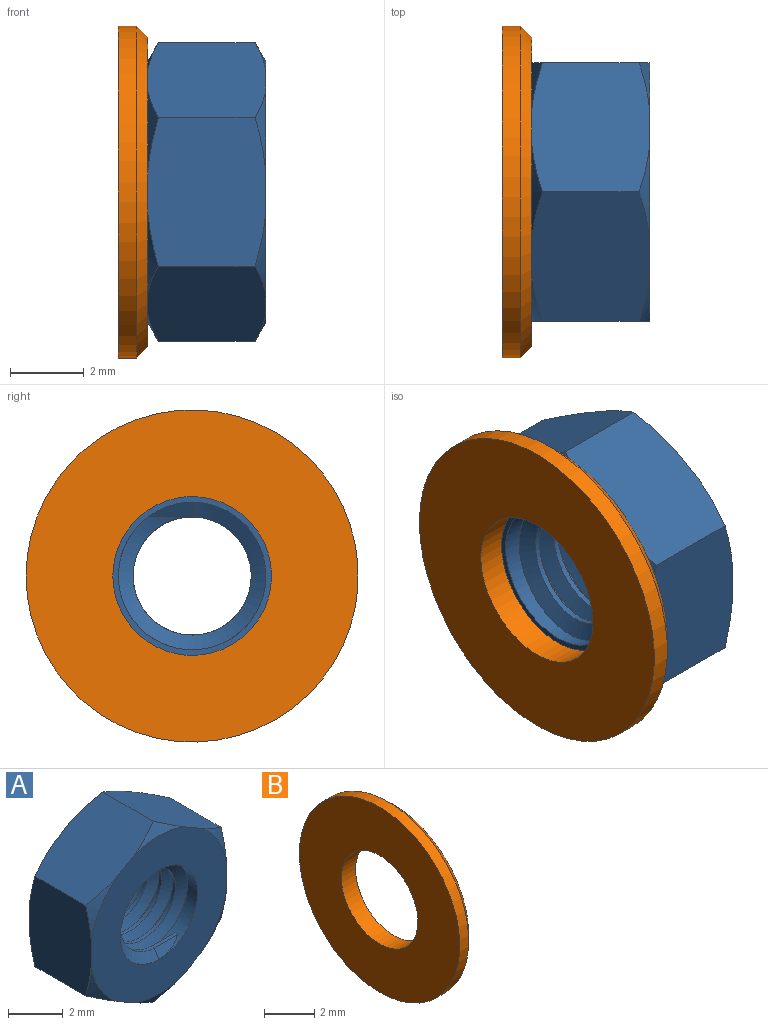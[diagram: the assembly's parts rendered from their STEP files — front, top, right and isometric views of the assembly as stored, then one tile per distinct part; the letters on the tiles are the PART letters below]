
ASSEMBLY  parts=2 mates=1
PART A: 28 faces, bbox 8.2x3.5x8.3 mm
  f0: cone r=3.54mm half-angle=60deg, axis (0,-1,0), area 0.8mm2, adj f11,f22,f23
  f1: cone r=3.54mm half-angle=60deg, axis (0,-1,0), area 0.8mm2, adj f11,f23,f24
  f2: cone r=3.54mm half-angle=60deg, axis (0,-1,0), area 0.8mm2, adj f11,f24,f25
  f3: cone r=3.54mm half-angle=60deg, axis (0,-1,0), area 0.8mm2, adj f11,f25,f26
  f4: cone r=3.54mm half-angle=60deg, axis (0,-1,0), area 0.8mm2, adj f11,f22,f27
  f5: cone r=4.04mm half-angle=60deg, axis (0,1,0), area 0.8mm2, adj f10,f22,f23
  f6: cone r=4.04mm half-angle=60deg, axis (0,1,0), area 0.8mm2, adj f10,f23,f24
  f7: cone r=4.04mm half-angle=60deg, axis (0,1,0), area 0.8mm2, adj f10,f24,f25
  f8: cone r=4.04mm half-angle=60deg, axis (0,1,0), area 0.8mm2, adj f10,f25,f26
  f9: cone r=4.04mm half-angle=60deg, axis (0,1,0), area 0.8mm2, adj f10,f26,f27
  f10: plane 7.08x7mm, normal (0,-1,0), area 26.7mm2, adj f5,f6,f7,f8,f9,f12,f21,f22
  f11: plane 7.08x7mm, normal (0,1,0), area 26.7mm2, adj f0,f1,f2,f3,f4,f12,f20,f22
  f12: cylinder r=2mm len=4mm, axis (0,1,0), area 11.1mm2, adj f10,f11,f13,f15,f16,f17,f18,f19
  f13: plane 0.62x0.38mm, normal (0.35,0,-0.94), area 0.2mm2, adj f12,f14,f15,f16
  f14: cylinder r=1.6mm len=3.2mm, axis (0,1,0), area 5.7mm2, adj f13,f15,f16,f17
  f15: bspline ~4.62x4mm, area 19.3mm2, adj f12,f13,f14,f18
  f16: bspline ~4.62x4mm, area 19.3mm2, adj f12,f13,f14,f19
  f17: plane 1.2x0.15mm, normal (0,0,1), area 0.2mm2, adj f12,f14,f18,f19
  f18: plane 1.31x0.51mm, normal (0,0.87,0.5), area 0.4mm2, adj f12,f15,f17
  f19: plane 1.31x0.51mm, normal (0,-0.87,0.5), area 0.4mm2, adj f12,f16,f17
  f20: cone r=3.54mm half-angle=60deg, axis (0,-1,0), area 0.8mm2, adj f11,f26,f27
  f21: cone r=4.04mm half-angle=60deg, axis (0,1,0), area 0.8mm2, adj f10,f22,f27
  f22: plane 3.68x3.38mm, normal (-0.5,0,0.87), area 12.2mm2, adj f0,f4,f5,f10,f11,f21,f23,f27
  f23: plane 3.68x3.38mm, normal (0.5,0,0.87), area 12.2mm2, adj f0,f1,f5,f6,f10,f11,f22,f24
  f24: plane 4.23x3.38mm, normal (1,0,0), area 12.2mm2, adj f1,f2,f6,f7,f10,f11,f23,f25
  f25: plane 3.68x3.38mm, normal (0.5,0,-0.87), area 12.2mm2, adj f2,f3,f7,f8,f10,f11,f24,f26
  f26: plane 3.68x3.38mm, normal (-0.5,0,-0.87), area 12.2mm2, adj f3,f8,f9,f10,f11,f20,f25,f27
  f27: plane 4.23x3.38mm, normal (-1,0,0), area 12.2mm2, adj f4,f9,f10,f11,f20,f21,f22,f26
PART B: 5 faces, bbox 0.8x9x9 mm
  f0: plane 9x9mm, normal (-1,0,0), area 49.1mm2, adj f1,f4
  f1: cylinder r=2.15mm len=4.3mm, axis (1,0,0), area 10.8mm2, adj f0,f2
  f2: plane 8.4x8.4mm, normal (1,0,0), area 40.9mm2, adj f1,f3
  f3: cone r=4.2mm half-angle=45deg, axis (-1,0,0), area 11.6mm2, adj f2,f4
  f4: cylinder r=4.5mm len=9mm, axis (1,0,0), area 14.1mm2, adj f0,f3
PLACE A rot(axis=(0.71,0.71,0),180deg) t=(4,0,0)mm
PLACE B at identity fixed
MATE fastened A.f0 <-> B.f1  axis (-1,0,0) through (0.8,0,0)mm
